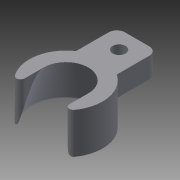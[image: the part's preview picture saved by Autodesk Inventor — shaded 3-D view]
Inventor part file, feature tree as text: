
AUTODESK INVENTOR PART (.ipt)
format: ipt  version: 2013 SP2 (Build 170200200, 200)  size: 136,192 bytes
history: native  units: mm
features: extrude x2, fillet x2, sketch x2, revolve x1
ambient origin geometry x8: Origin, YZ Plane, XZ Plane, XY Plane, X Axis, Y Axis, Z Axis, Center Point
bodies: Solid1 (feature_tree)
feature tree (7):
  revolve  "Revolution1"  [1 undecoded]
  extrude  "Extrusion1"  Depth=5.5mm
  fillet  "Fillet1"  Radius=10.0mm
  extrude  "Extrusion2"  Depth=10.0mm TaperAngle=0.0deg
  fillet  "Fillet2"  Radius=1.0mm
  sketch  "Sketch3"  dims[d7=90.0deg d11=0.0mm]
  sketch  "Sketch4"  dims[d13=9.0mm d14=5.5mm d15=10.0mm d16=10.0mm d17=0.0mm d18=1.0mm d19=10.0mm d21=10.0mm d22=3.2mm d23=5.0mm d24=0.0mm d25=2.0mm d26=8.5mm d29=4.41345mm]
note: 1 required parameter value undecoded (feature->parameter linkage not recoverable at this tier; creation-order binding heuristic only, values carry confidence <= 0.55)
